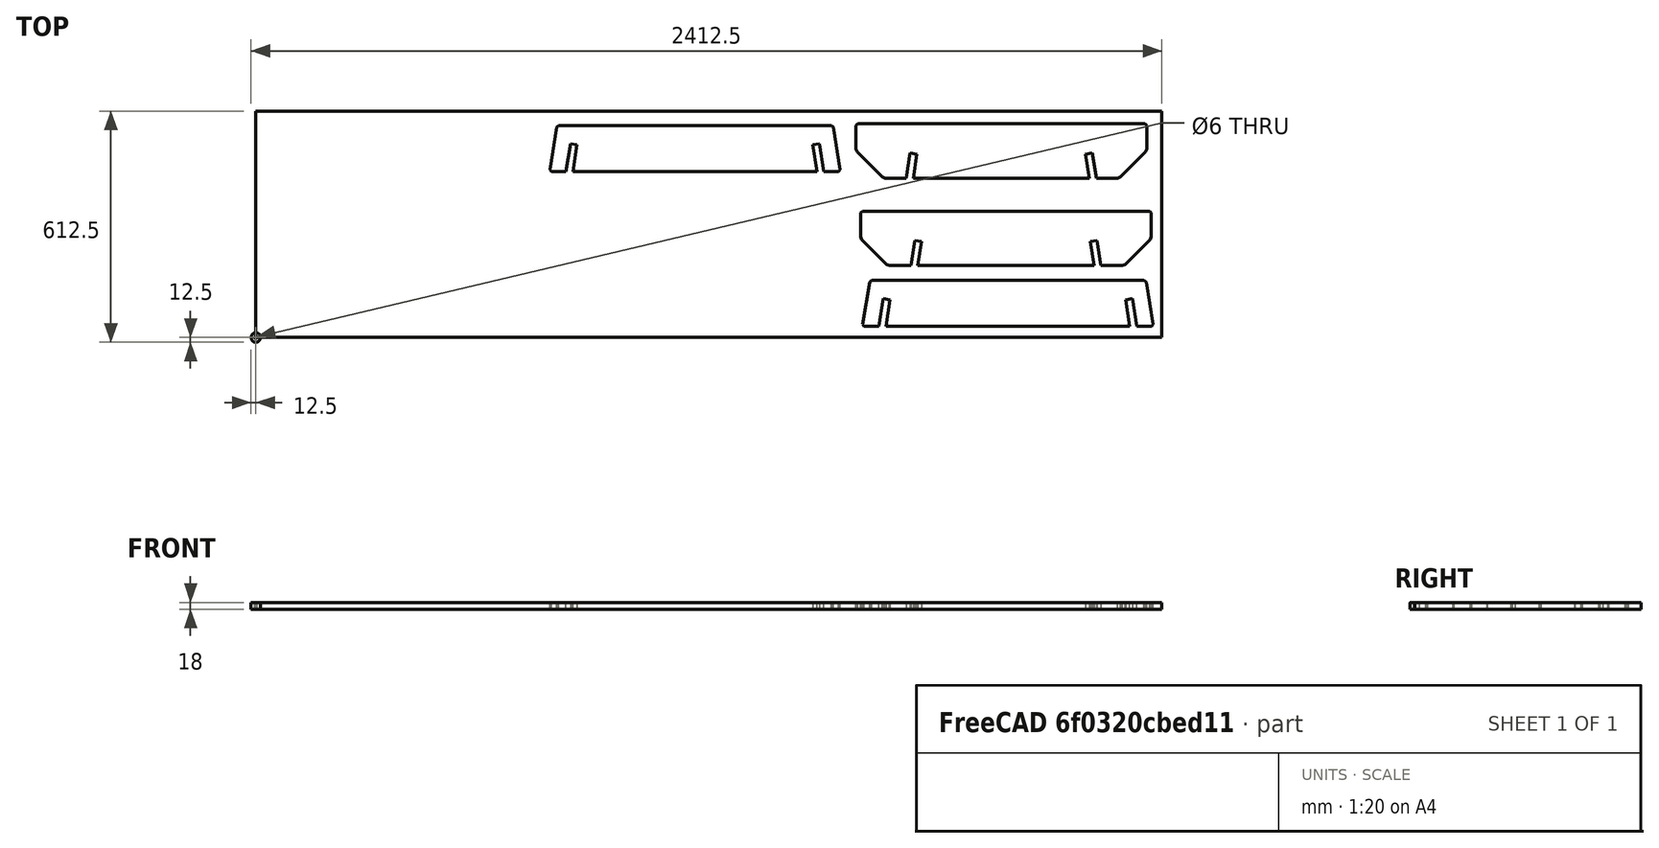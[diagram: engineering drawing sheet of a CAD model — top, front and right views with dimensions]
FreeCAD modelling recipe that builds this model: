
FCSTD DOCUMENT  (FreeCAD 0.18R4 (GitTag))
Label: Parahorse test mill
License: CreativeCommons Attribution-ShareAlike
LicenseURL: http://creativecommons.org/licenses/by-sa/4.0/
objects: Part::FeaturePython×9, Part::Feature×8, Path::FeaturePython×8, Part::Cylinder×2, Part::Box×1, App::FeaturePython×1, App::DocumentObjectGroup×1, Path::FeatureCompoundPython×1, Part::Cut×1
note: 23 computed .brp shape members not serialized (recipe doc carries the construction recipe); baked Part::Feature solids carry a one-line shape summary decoded from their .brp

FEATURE [Part::Feature] Clone002002  label="Nested bottom bar001"
  Placement = pos=(1607.39,-28.1682,9) rot=(-1,0,0;1.5708rad)
  shape: bbox 768.6 x 121.6 x 18 mm, 18 faces (baked)
FEATURE [Part::Feature] Clone002001  label="Nested top bar001"
  Placement = pos=(1602.41,-431.131,9) rot=(-1,0,0;1.5708rad)
  shape: bbox 770 x 144.4 x 18 mm, 22 faces (baked)
FEATURE [Part::Feature] Array003001  label="Nested leg004"
  Placement = pos=(822.639,638.32,1.3e-14) rot=(0,0,1;3.05433rad)
  shape: bbox 771 x 232.8 x 18 mm, 32 faces (baked)
FEATURE [Part::Feature] Array002001  label="Nested leg003"
  Placement = pos=(45.007,152.852,1.5e-14) rot=(0.043578,0.998099,-0.043578;1.5727rad)
  shape: bbox 771 x 232.8 x 18 mm, 32 faces (baked)
FEATURE [Part::Feature] Array003002  label="Nested leg005"
  Placement = pos=(834.04,145.63,1.5e-14) rot=(0.043578,0.998099,-0.043578;1.5727rad)
  shape: bbox 771 x 232.8 x 18 mm, 32 faces (baked)
FEATURE [Part::Feature] Array003003  label="Nested leg006"
  Placement = pos=(1626.46,625.012,8e-15) rot=(0,0,1;3.05433rad)
  shape: bbox 771 x 232.8 x 18 mm, 32 faces (baked)
FEATURE [Part::Feature] Clone002003  label="Nested top bar002"
  Placement = pos=(1590,-193.118,9) rot=(-1,0,0;1.5708rad)
  shape: bbox 770 x 144.4 x 18 mm, 22 faces (baked)
FEATURE [Part::Feature] Clone002004  label="Nested bottom bar002"
  Placement = pos=(778.166,390.377,9) rot=(-1,0,0;1.5708rad)
  shape: bbox 768.6 x 121.6 x 18 mm, 18 faces (baked)
FEATURE [Part::Box] Box  label="Material to mill"
  AttacherType = Attacher::AttachEngine3D
  Height = 18
  Length = 2400
  Width = 600
FEATURE [App::FeaturePython] SetupSheet  # Path/CAM operation (typed FeaturePython)
  ClearanceHeightExpression = OpStockZMax+SetupSheet.ClearanceHeightOffset
  ClearanceHeightOffset = 6
  FinalDepthExpression = OpFinalDepth
  HorizRapid = 250
  SafeHeightExpression = OpStockZMax+SetupSheet.SafeHeightOffset
  SafeHeightOffset = 6
  StartDepthExpression = OpStartDepth
  StepDownExpression = OpToolDiameter
  VertRapid = 60
FEATURE [Part::FeaturePython] Clone  label="Model-Nested bottom bar001"  # Draft clone (typed FeaturePython)
  AttacherType = Attacher::AttachEngine3D
  Fuse = false
  Objects = -> [Clone002002]
  PathResource = Model
  Placement = pos=(1607.39,-20.1682,9) rot=(-1,0,0;1.5708rad)
  Scale = (1,1,1)
FEATURE [Part::FeaturePython] Clone002005  label="Model-Nested bottom bar002"  # Draft clone (typed FeaturePython)
  AttacherType = Attacher::AttachEngine3D
  Fuse = false
  Objects = -> [Clone002004]
  PathResource = Model
  Placement = pos=(778.166,390.377,9) rot=(-1,0,0;1.5708rad)
  Scale = (1,1,1)
FEATURE [Part::FeaturePython] Clone002006  label="Model-Nested leg003"  # Draft clone (typed FeaturePython)
  AttacherType = Attacher::AttachEngine3D
  Fuse = false
  Objects = -> [Array002001]
  PathResource = Model
  Placement = pos=(45.007,152.852,1.5e-14) rot=(0.043578,0.998099,-0.043578;1.5727rad)
  Scale = (1,1,1)
FEATURE [Part::FeaturePython] Clone002007  label="Model-Nested leg004"  # Draft clone (typed FeaturePython)
  AttacherType = Attacher::AttachEngine3D
  Fuse = false
  Objects = -> [Array003001]
  PathResource = Model
  Placement = pos=(822.639,638.32,1.3e-14) rot=(0,0,1;3.05433rad)
  Scale = (1,1,1)
FEATURE [Part::FeaturePython] Clone002008  label="Model-Nested leg005"  # Draft clone (typed FeaturePython)
  AttacherType = Attacher::AttachEngine3D
  Fuse = false
  Objects = -> [Array003002]
  PathResource = Model
  Placement = pos=(827.04,145.63,1.5e-14) rot=(0.043578,0.998099,-0.043578;1.5727rad)
  Scale = (1,1,1)
FEATURE [Part::FeaturePython] Clone002009  label="Model-Nested leg006"  # Draft clone (typed FeaturePython)
  AttacherType = Attacher::AttachEngine3D
  Fuse = false
  Objects = -> [Array003003]
  PathResource = Model
  Placement = pos=(1626.46,625.012,8e-15) rot=(0,0,1;3.05433rad)
  Scale = (1,1,1)
FEATURE [Part::FeaturePython] Clone002010  label="Model-Nested top bar001"  # Draft clone (typed FeaturePython)
  AttacherType = Attacher::AttachEngine3D
  Fuse = false
  Objects = -> [Clone002001]
  PathResource = Model
  Placement = pos=(1602.41,-425.131,9) rot=(-1,0,0;1.5708rad)
  Scale = (1,1,1)
FEATURE [Part::FeaturePython] Clone002011  label="Model-Nested top bar002"  # Draft clone (typed FeaturePython)
  AttacherType = Attacher::AttachEngine3D
  Fuse = false
  Objects = -> [Clone002003]
  PathResource = Model
  Placement = pos=(1590,-193.118,9) rot=(-1,0,0;1.5708rad)
  Scale = (1,1,1)
FEATURE [App::DocumentObjectGroup] Model
  Group = -> [Clone,Clone002005,Clone002006,Clone002007,Clone002008,Clone002009,Clone002010,Clone002011]
FEATURE [Path::FeaturePython] T1__6mm_upcut  label="T1: 6mm upcut"  # Path/CAM operation (typed FeaturePython)
  HorizFeed = 60
  HorizRapid = 250
  SpindleDir = 0
  SpindleSpeed = 18000
  ToolNumber = 1
  VertFeed = 25
  VertRapid = 60
  expr: HorizRapid = SetupSheet.HorizRapid
  expr: VertRapid = SetupSheet.VertRapid
FEATURE [Path::FeaturePython] Contour  label="Contour - outside cut"  # Path/CAM operation (typed FeaturePython)
  Active = true
  AreaParams:
    Tolerance = 1e-07
    FitArcs = True
    Simplify = False
    CleanDistance = 0.0
    Accuracy = 0.01
    Unit = 1.0
    MinArcPoints = 4
    MaxArcPoints = 100
    ClipperScale = 10000000.0
    Fill = 0
    Coplanar = 2
    Reorient = True
    Outline = False
    Explode = False
    OpenMode = 0
    Deflection = 0.01
    SubjectFill = 0
    ClipFill = 0
    Offset = 3.0
    ExtraPass = 0
    Stepover = 0.0
    LastStepover = 0.0
    JoinType = 0
    EndType = 0
    MiterLimit = 2.0
    RoundPrecision = 0.0
    PocketMode = 0
    ToolRadius = 1.0
    PocketExtraOffset = 0.0
    PocketStepover = 0.0
    PocketLastStepover = 0.0
    FromCenter = False
    Angle = 45.0
    AngleShift = 0.0
    Shift = 0.0
    Thicken = False
    SectionCount = -1
    Stepdown = 1.0
    SectionOffset = 0.0
    SectionTolerance = 1e-06
    SectionMode = 2
    Project = False
  ClearanceHeight = 24
  Direction = 1
  FinalDepth = -0.5
  JoinType = 0
  MiterLimit = 0.1
  OffsetExtra = 0
  OpFinalDepth = 0
  OpStartDepth = 18
  OpStockZMax = 18
  OpStockZMin = 0
  OpToolDiameter = 6
  PathParams = {'orientation': 0, 'feedrate': 60.0, 'feedrate_v': 25.0, 'verbose': True, 'resume_height': 24.0, 'retraction': 24.0, 'return_end': True, 'preamble': False}
  SafeHeight = 24
  Side = 0
  StartDepth = 18
  StartPoint = (0,0,0)
  StepDown = 19
  ToolController = -> T1__6mm_upcut
  UseComp = true
  UseStartPoint = false
  expr: ClearanceHeight = OpStockZMax + SetupSheet.ClearanceHeightOffset
  expr: SafeHeight = OpStockZMax + SetupSheet.SafeHeightOffset
  expr: StepDown = 19
  expr: FinalDepth = -0.5
  expr: StartDepth = 18
FEATURE [Path::FeaturePython] DogboneDressup  # Path/CAM operation (typed FeaturePython)
  Base = -> Contour
  Custom = 0
  Incision = 0
  Side = 0
  Style = 0
FEATURE [Path::FeaturePython] RampEntryDressup  label="Outside cut with ramp"  # Path/CAM operation (typed FeaturePython)
  Angle = 60
  Base = -> DogboneDressup
  CustomFeedRate = 0
  DressupStartDepth = 18
  Method = 2
  RampFeedRate = 0
  UseStartDepth = true
FEATURE [Path::FeaturePython] Profile_Edges  # Path/CAM operation (typed FeaturePython)
  Active = true
  AreaParams:
    Tolerance = 1e-07
    FitArcs = True
    Simplify = False
    CleanDistance = 0.0
    Accuracy = 0.01
    Unit = 1.0
    MinArcPoints = 4
    MaxArcPoints = 100
    ClipperScale = 10000000.0
    Fill = 0
    Coplanar = 0
    Reorient = True
    Outline = False
    Explode = False
    OpenMode = 0
    Deflection = 0.01
    SubjectFill = 0
    ClipFill = 0
    Offset = -3.0
    ExtraPass = 0
    Stepover = 0.0
    LastStepover = 0.0
    JoinType = 0
    EndType = 0
    MiterLimit = 2.0
    RoundPrecision = 0.0
    PocketMode = 0
    ToolRadius = 1.0
    PocketExtraOffset = 0.0
    PocketStepover = 0.0
    PocketLastStepover = 0.0
    FromCenter = False
    Angle = 45.0
    AngleShift = 0.0
    Shift = 0.0
    Thicken = False
    SectionCount = -1
    Stepdown = 1.0
    SectionOffset = 0.0
    SectionTolerance = 1e-06
    SectionMode = 2
    Project = False
  Base = -> [Clone002006,Clone002007,Clone002008,Clone002009]
  ClearanceHeight = 24
  Direction = 0
  FinalDepth = -0.5
  JoinType = 0
  MiterLimit = 0.1
  OffsetExtra = 0
  OpFinalDepth = 18
  OpStartDepth = 37
  OpStockZMax = 18
  OpStockZMin = 0
  OpToolDiameter = 6
  PathParams = {'orientation': 1, 'feedrate': 60.0, 'feedrate_v': 25.0, 'verbose': True, 'resume_height': 24.0, 'retraction': 24.0, 'return_end': True, 'preamble': False}
  SafeHeight = 24
  Side = 1
  StartDepth = 18
  StartPoint = (0,0,0)
  StepDown = 19
  ToolController = -> T1__6mm_upcut
  UseComp = true
  UseStartPoint = false
  expr: ClearanceHeight = OpStockZMax + SetupSheet.ClearanceHeightOffset
  expr: SafeHeight = OpStockZMax + SetupSheet.SafeHeightOffset
  expr: StepDown = 19
  expr: FinalDepth = -0.5
  expr: StartDepth = 18
FEATURE [Part::FeaturePython] Clone002012  label="Stock-Material to mill"  # Draft clone (typed FeaturePython)
  AttacherType = Attacher::AttachEngine3D
  Fuse = false
  Objects = -> [Box]
  PathResource = Stock
  Scale = (1,1,1)
  StockType = Unknown
FEATURE [Path::FeaturePython] DogboneDressup001  # Path/CAM operation (typed FeaturePython)
  Base = -> Profile_Edges
  Custom = 4
  Incision = 0
  Side = 0
  Style = 0
FEATURE [Path::FeaturePython] RampEntryDressup001  label="Inside cut with ramp"  # Path/CAM operation (typed FeaturePython)
  Angle = 60
  Base = -> DogboneDressup001
  CustomFeedRate = 0
  DressupStartDepth = 18
  Method = 2
  RampFeedRate = 0
  UseStartDepth = true
FEATURE [Path::FeatureCompoundPython] Operations  # Path/CAM operation (typed FeaturePython)
  Group = -> [RampEntryDressup001,RampEntryDressup]
  UsePlacements = false
FEATURE [Path::FeaturePython] Job  # Path/CAM operation (typed FeaturePython)
  GeometryTolerance = 0.01
  Model = -> Model
  Operations = -> Operations
  PostProcessor = 7
  PostProcessorOutputFile = <path> sawhorse/Test milling/Parahorsemill.sbp
  SetupSheet = -> SetupSheet
  Stock = -> Clone002012
  ToolController = -> [T1__6mm_upcut]
FEATURE [Part::Cylinder] Cylinder
  Angle = 360
  AttacherType = Attacher::AttachEngine3D
  Height = 18
  Radius = 12.5
FEATURE [Part::Cylinder] Cylinder001
  Angle = 360
  AttacherType = Attacher::AttachEngine3D
  Height = 18
  Radius = 3
FEATURE [Part::Cut] Cut  label="Hole drill"
  Base = -> Cylinder
  Tool = -> Cylinder001
note: 1 file-system path scrubbed to <path> (originals preserved in the JSON sidecar)
